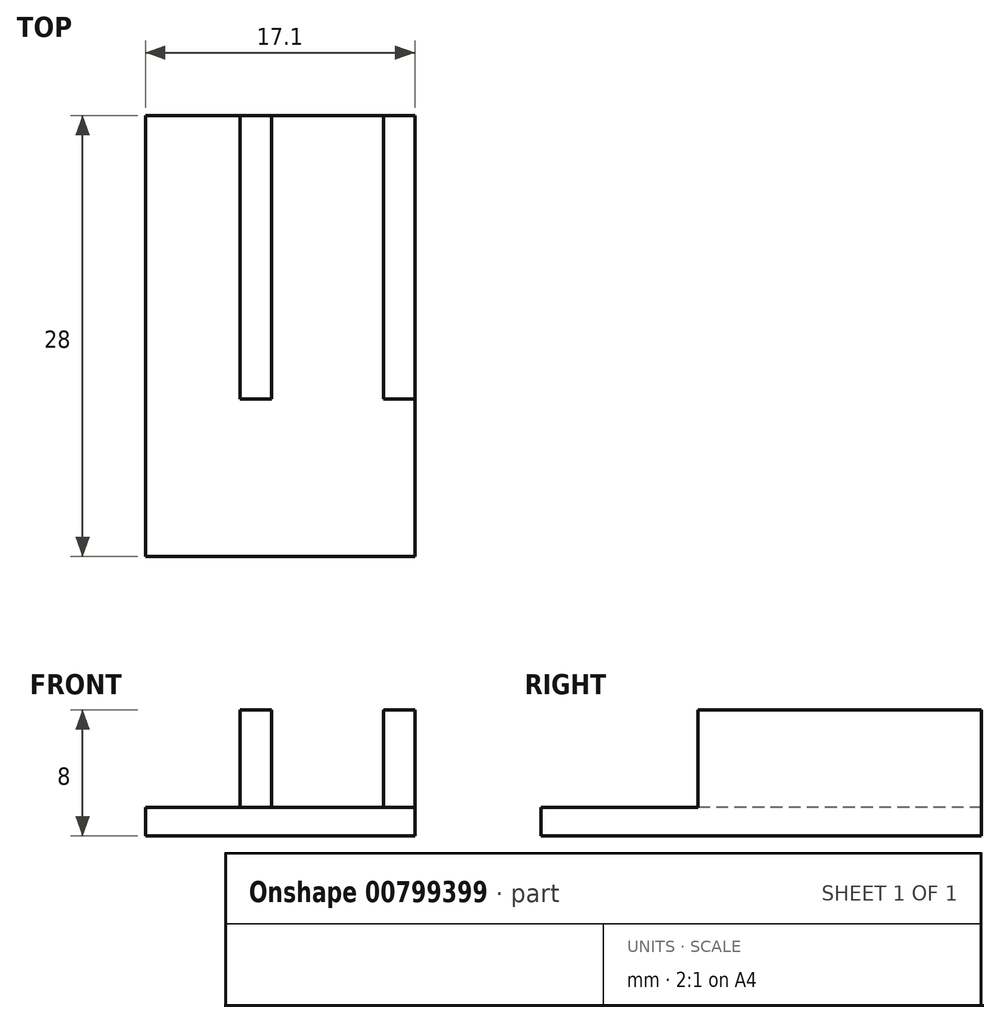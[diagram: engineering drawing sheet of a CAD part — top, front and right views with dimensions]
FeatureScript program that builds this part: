
annotation { "Feature Type Name" : "Feature", "Feature Type Description" : "" }
export const myFeature = defineFeature(function(context is Context, id is Id, definition is map)
    precondition{}
    {
        {
            var Q0;
            Q0=qCreatedBy(makeId("Top.planeOp"),FACE);
            var sketch = newSketch(context, id + "F0", { "sketchPlane" : qUnion([Q0])});
            skLineSegment(sketch, "E0.bottom", {"start": v(3.55, -9) * mm, "end": v(-3.55, -9) * mm});
            skLineSegment(sketch, "E0.top", {"start": v(3.55, 9) * mm, "end": v(-3.55, 9) * mm});
            skLineSegment(sketch, "E0.left", {"start": v(3.55, -9) * mm, "end": v(3.55, 9) * mm});
            skLineSegment(sketch, "E0.right", {"start": v(-3.55, -9) * mm, "end": v(-3.55, 9) * mm});
            skPoint(sketch, "E0.middle", {"position": v(0, 0) * mm});
            skLineSegment(sketch, "E1.bottom", {"start": v(-3.55, 9) * mm, "end": v(-5.55, 9) * mm});
            skLineSegment(sketch, "E1.top", {"start": v(-3.55, -9) * mm, "end": v(-5.55, -9) * mm});
            skLineSegment(sketch, "E1.left", {"start": v(-3.55, 9) * mm, "end": v(-3.55, -9) * mm});
            skLineSegment(sketch, "E1.right", {"start": v(-5.55, 9) * mm, "end": v(-5.55, -9) * mm});
            skLineSegment(sketch, "E2.bottom", {"start": v(3.55, 9) * mm, "end": v(5.55, 9) * mm});
            skLineSegment(sketch, "E2.top", {"start": v(3.55, -9) * mm, "end": v(5.55, -9) * mm});
            skLineSegment(sketch, "E2.left", {"start": v(3.55, 9) * mm, "end": v(3.55, -9) * mm});
            skLineSegment(sketch, "E2.right", {"start": v(5.55, 9) * mm, "end": v(5.55, -9) * mm});
            skLineSegment(sketch, "E3.bottom", {"start": v(-5.55, -9) * mm, "end": v(5.55, -9) * mm});
            skLineSegment(sketch, "E3.top", {"start": v(-5.55, -19) * mm, "end": v(5.55, -19) * mm});
            skLineSegment(sketch, "E3.left", {"start": v(-5.55, -9) * mm, "end": v(-5.55, -19) * mm});
            skLineSegment(sketch, "E3.right", {"start": v(5.55, -9) * mm, "end": v(5.55, -19) * mm});
            skLineSegment(sketch, "E4.left", {"start": v(-5.55, 9) * mm, "end": v(-5.55, -19) * mm});
            skLineSegment(sketch, "E5.left", {"start": v(5.55, 9) * mm, "end": v(5.55, -19) * mm});
            skLineSegment(sketch, "E6.bottom", {"start": v(-5.55, 9) * mm, "end": v(-11.55, 9) * mm});
            skLineSegment(sketch, "E6.top", {"start": v(-5.55, -19) * mm, "end": v(-11.55, -19) * mm});
            skLineSegment(sketch, "E6.right", {"start": v(-11.55, 9) * mm, "end": v(-11.55, -19) * mm});
            skSolve(sketch);
        }
        {
            var Q0;
            Q0=makeQuery(id+"F0.imprint","IMPRINT",FACE,{"disambiguationData":[TD([[makeQuery(id+"F0.imprint","IMPRINT",EDGE,{"derivedFrom":sQuery(id+"F0.wireOp",EDGE,"E3.top")}),1.0]])]});
            var Q1;
            Q1=makeQuery(id+"F0.imprint","IMPRINT",FACE,{"disambiguationData":[TD([[makeQuery(id+"F0.imprint","IMPRINT",EDGE,{"derivedFrom":sQuery(id+"F0.wireOp",EDGE,"E0.top")}),1.0]])]});
            var Q2;
            {var subQ3=sQuery(id+"F0.wireOp",EDGE,"E4.bottom");Q2=makeQuery(id+"F0.imprint","IMPRINT",FACE,{"disambiguationData":[TD([[makeQuery(id+"F0.imprint","IMPRINT",EDGE,{"derivedFrom":subQ3}),1.0]])]});}
            var Q3;
            {var subQ3=sQuery(id+"F0.wireOp",EDGE,"E5.bottom");Q3=makeQuery(id+"F0.imprint","IMPRINT",FACE,{"disambiguationData":[TD([[makeQuery(id+"F0.imprint","IMPRINT",EDGE,{"derivedFrom":subQ3}),-1.0]])]});}
            var Q4;
            {var subQ3=sQuery(id+"F0.wireOp",EDGE,"E6.bottom");Q4=makeQuery(id+"F0.imprint","IMPRINT",FACE,{"disambiguationData":[TD([[makeQuery(id+"F0.imprint","IMPRINT",EDGE,{"derivedFrom":subQ3}),1.0]])]});}
            extrude(context, id + "F1", {"entities" : qUnion([Q0, Q1, Q2, Q3, Q4]), "depth" : 1.8 * mm, "offsetDistance" : 25 * mm});
        }
        {
            var Q0;
            Q0=makeQuery(id+"F0.imprint","IMPRINT",FACE,{"disambiguationData":[TD([[makeQuery(id+"F0.imprint","IMPRINT",EDGE,{"derivedFrom":sQuery(id+"F0.wireOp",EDGE,"E1.bottom")}),1.0]])]});
            var Q1;
            Q1=makeQuery(id+"F0.imprint","IMPRINT",FACE,{"disambiguationData":[TD([[makeQuery(id+"F0.imprint","IMPRINT",EDGE,{"derivedFrom":sQuery(id+"F0.wireOp",EDGE,"E2.bottom")}),-1.0]])]});
            extrude(context, id + "F2", {"entities" : qUnion([Q0, Q1]), "operationType" : NewBodyOperationType.ADD, "depth" : 8 * mm, "offsetDistance" : 25 * mm});
        }
    });
